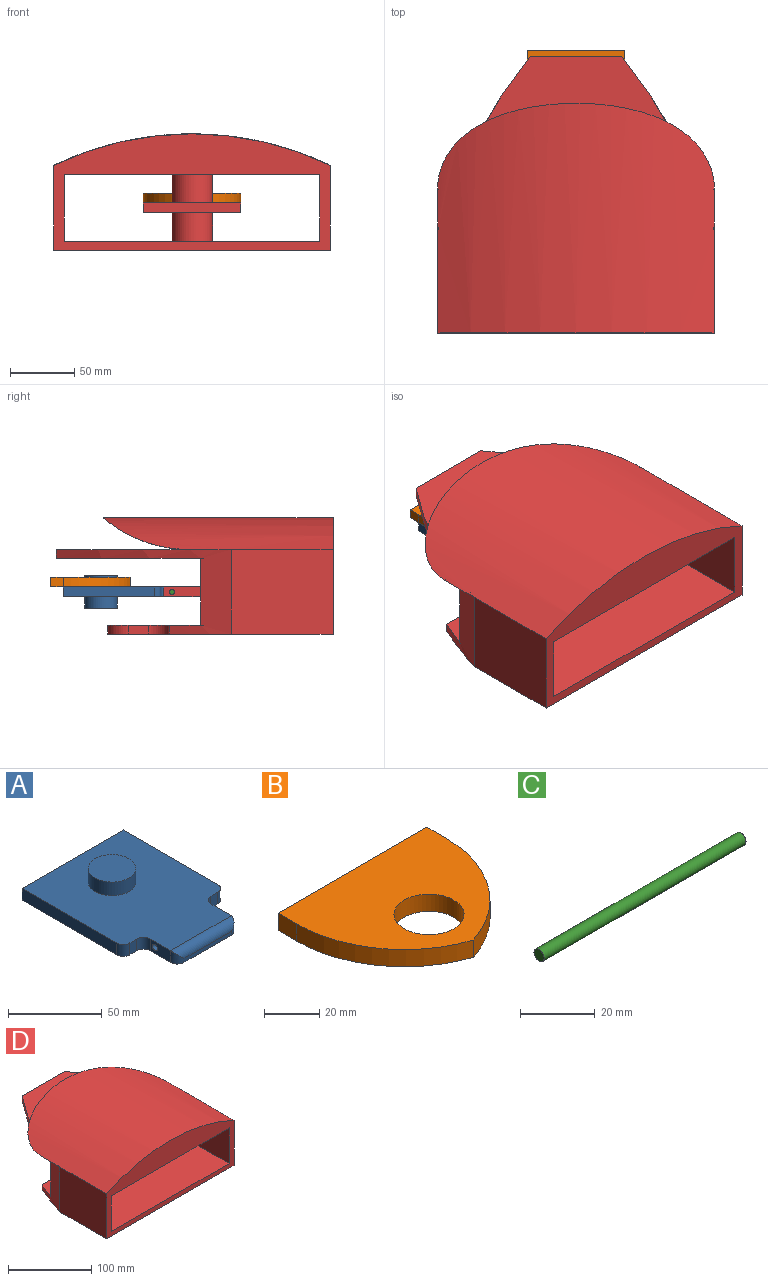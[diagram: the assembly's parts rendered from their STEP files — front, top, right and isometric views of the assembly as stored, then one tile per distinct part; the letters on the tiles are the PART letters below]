
ASSEMBLY  parts=4 mates=3
PART A: 22 faces, bbox 76.2x101.6x25.4 mm
  f0: plane 76.2x7.62mm, normal (0,1,0), area 580.6mm2, adj f1,f7,f8,f9
  f1: plane 71.12x7.62mm, normal (-1,0,0), area 541.9mm2, adj f0,f8,f9,f15
  f2: plane 7.62x5.08mm, normal (0,-1,0), area 38.7mm2, adj f8,f9,f15,f20
  f3: plane 15.24x7.62mm, normal (-1,0,0), area 104.1mm2, adj f8,f9,f14,f18,f20
  f4: plane 35.56x2.54mm, normal (0,-1,0), area 90.3mm2, adj f9,f16,f17,f18
  f5: plane 15.24x7.62mm, normal (1,0,0), area 104.1mm2, adj f8,f9,f14,f16,f21
  f6: plane 7.62x5.08mm, normal (0,-1,0), area 38.7mm2, adj f8,f9,f19,f21
  f7: plane 71.12x7.62mm, normal (1,0,0), area 541.9mm2, adj f0,f8,f9,f19
  f8: plane 96.52x76.2mm, normal (0,0,1), area 6229.7mm2, adj f0,f1,f2,f3,f5,f6,f7,f12
  f9: plane 101.6x76.2mm, normal (0,0,-1), area 6450.9mm2, adj f0,f1,f2,f3,f4,f5,f6,f7
  f10: plane 25.38x25.38mm, normal (0,0,-1), area 505.8mm2, adj f11
  f11: cylinder r=12.69mm len=25.38mm, axis (0,0,-1), area 708.7mm2, adj f9,f10
  f12: cylinder r=12.69mm len=25.38mm, axis (0,0,-1), area 708.7mm2, adj f8,f13
  f13: plane 25.38x25.38mm, normal (0,0,1), area 505.8mm2, adj f12
  f14: cylinder r=1.96mm len=45.72mm, axis (1,0,0), area 561.8mm2, adj f3,f5
  f15: cylinder r=5.08mm len=7.62mm, axis (0,0,-1), area 60.8mm2, adj f1,f2,f8,f9
  f16: cylinder r=5.08mm len=7.62mm, axis (0,0,1), area 46.1mm2, adj f4,f5,f9,f17
  f17: cylinder r=5.08mm len=45.72mm, axis (-1,0,0), area 335.4mm2, adj f4,f8,f16,f18
  f18: cylinder r=5.08mm len=7.62mm, axis (0,0,-1), area 46.1mm2, adj f3,f4,f9,f17
  f19: cylinder r=5.08mm len=7.62mm, axis (0,0,-1), area 60.8mm2, adj f6,f7,f8,f9
  f20: cylinder r=5.08mm len=7.62mm, axis (0,0,1), area 60.8mm2, adj f2,f3,f8,f9
  f21: cylinder r=5.08mm len=7.62mm, axis (0,0,1), area 60.8mm2, adj f5,f6,f8,f9
PART B: 8 faces, bbox 76.2x61.9x7.6 mm
  f0: plane 9.51x7.62mm, normal (-1,0,0), area 72.5mm2, adj f1,f5,f6,f7
  f1: cylinder r=55.09mm len=52.4mm, axis (0,0,-1), area 527.8mm2, adj f0,f2,f6,f7
  f2: cylinder r=55.09mm len=52.4mm, axis (0,0,-1), area 527.8mm2, adj f1,f3,f6,f7
  f3: plane 9.51x7.62mm, normal (1,0,0), area 72.5mm2, adj f2,f5,f6,f7
  f4: cylinder r=12.69mm len=25.38mm, axis (0,0,-1), area 607.5mm2, adj f6,f7
  f5: plane 76.2x7.62mm, normal (0,1,0), area 580.6mm2, adj f0,f3,f6,f7
  f6: plane 76.2x61.92mm, normal (0,0,1), area 3144.5mm2, adj f0,f1,f2,f3,f4,f5
  f7: plane 76.2x61.92mm, normal (0,0,-1), area 3144.5mm2, adj f0,f1,f2,f3,f4,f5
PART C: 3 faces, bbox 76.2x3.8x3.8 mm
  f0: cylinder r=1.91mm len=76.2mm, axis (-1,0,0), area 912.1mm2, adj f1,f2
  f1: plane 3.81x3.81mm, normal (1,0,0), area 11.4mm2, adj f0
  f2: plane 3.81x3.81mm, normal (-1,0,0), area 11.4mm2, adj f0
PART D: 36 faces, bbox 215.9x215.7x90.8 mm
  f0: plane 192.64x103.63mm, normal (0,0,1), area 14383.3mm2, adj f17,f18,f27,f35
  f1: plane 215.92x175.67mm, normal (0,0,-1), area 27802.2mm2, adj f15,f16,f17,f18,f19,f20,f28,f29
  f2: plane 25.4x7.62mm, normal (1,0,0), area 181.5mm2, adj f3,f9,f10,f11,f13
  f3: plane 12.95x7.62mm, normal (0,1,0), area 98.7mm2, adj f2,f4,f10,f11
  f4: plane 73.91x7.62mm, normal (-1,0,0), area 551.2mm2, adj f3,f5,f10,f11,f13
  f5: plane 76.2x7.62mm, normal (0,-1,0), area 580.6mm2, adj f4,f6,f10,f11
  f6: plane 73.91x7.62mm, normal (1,0,0), area 551.2mm2, adj f5,f7,f10,f11,f12
  f7: plane 12.95x7.62mm, normal (0,1,0), area 98.7mm2, adj f6,f8,f10,f11
  f8: plane 25.4x7.62mm, normal (-1,0,0), area 181.5mm2, adj f7,f9,f10,f11,f12
  f9: plane 50.29x7.62mm, normal (0,1,0), area 383.2mm2, adj f2,f8,f10,f11
  f10: plane 76.2x73.91mm, normal (0,0,1), area 3550.4mm2, adj f2,f3,f4,f5,f6,f7,f8,f9
  f11: plane 76.2x73.91mm, normal (0,0,-1), area 3550.4mm2, adj f2,f3,f4,f5,f6,f7,f8,f9
  f12: cylinder r=1.96mm len=12.95mm, axis (1,0,0), area 159.2mm2, adj f6,f8
  f13: cylinder r=1.96mm len=12.95mm, axis (1,0,0), area 159.2mm2, adj f2,f4
  f14: cylinder r=16mm len=32mm, axis (0,0,1), area 2242.7mm2, adj f11,f24
  f15: cylinder r=15.95mm len=31.9mm, axis (0,0,-1), area 25.5mm2, adj f1,f26
  f16: plane 215.92x90.76mm, normal (0,-1,0), area 7432mm2, adj f1,f19,f20,f21,f22,f23,f24,f34
  f17: cylinder r=413.42mm len=136.38mm, axis (0,0,-1), area 3060.6mm2, adj f0,f1,f20,f22,f23,f24,f27,f30
  f18: cylinder r=413.42mm len=136.38mm, axis (0,0,-1), area 2749.8mm2, adj f0,f1,f19,f21,f23,f24,f27,f29
  f19: plane 79.37x66.04mm, normal (-1,0,0), area 5241.7mm2, adj f1,f16,f18,f34
  f20: plane 79.37x66.04mm, normal (1,0,0), area 5241.7mm2, adj f1,f16,f17,f34
  f21: plane 103.26x52.23mm, normal (1,0,0), area 5393.4mm2, adj f16,f18,f23,f24
  f22: plane 103.26x52.23mm, normal (-1,0,0), area 5393.4mm2, adj f16,f17,f23,f24
  f23: plane 215.75x199.55mm, normal (0,0,-1), area 35921.8mm2, adj f16,f17,f18,f21,f22,f25,f27
  f24: plane 199.55x175.67mm, normal (0,0,1), area 26296.2mm2, adj f14,f16,f17,f18,f21,f22,f28,f29
  f25: cylinder r=16mm len=32mm, axis (0,0,1), area 2242.7mm2, adj f10,f23
  f26: plane 31.9x31.9mm, normal (0,0,-1), area 799.4mm2, adj f15
  f27: plane 71.4x6.9mm, normal (0,1,0), area 493mm2, adj f0,f17,f18,f23
  f28: plane 15.85x6.9mm, normal (-1,0,0), area 109.5mm2, adj f1,f24,f30,f31
  f29: plane 112.74x6.9mm, normal (0,1,0), area 778.4mm2, adj f1,f18,f24,f31
  f30: cylinder r=15.94mm len=29.67mm, axis (0,0,-1), area 287.1mm2, adj f1,f17,f24,f28
  f31: cylinder r=15.94mm len=15.94mm, axis (0,0,1), area 172.9mm2, adj f1,f24,f28,f29
  f32: plane 32.75x11.64mm, normal (0,0,-1), area 182.1mm2, adj f18,f34,f35
  f33: plane 32.75x11.64mm, normal (0,0,-1), area 182.1mm2, adj f17,f34,f35
  f34: cylinder r=248.09mm len=215.92mm, axis (0,-1,0), area 36964.3mm2, adj f16,f19,f20,f32,f33,f35
  f35: cylinder r=103.02mm len=215.92mm, axis (-1,0,0), area 12374.4mm2, adj f0,f32,f33,f34
PLACE A t=(156.86,25.47,-45.52)mm
PLACE B t=(-34.14,28.22,-37.9)mm
PLACE C t=(156.86,25.47,-45.52)mm
PLACE D t=(156.86,25.47,-45.52)mm fixed
MATE revolute A.f11 <-> B.f4  axis (0,0,1) through (156.86,50.55,-41.71)mm
MATE fastened D.f12 <-> C.f0  axis (-1,0,0) through (118.76,-4.6,-45.52)mm
MATE revolute C.f0 <-> A.f14  axis (-1,0,0) through (156.86,-4.6,-45.52)mm
